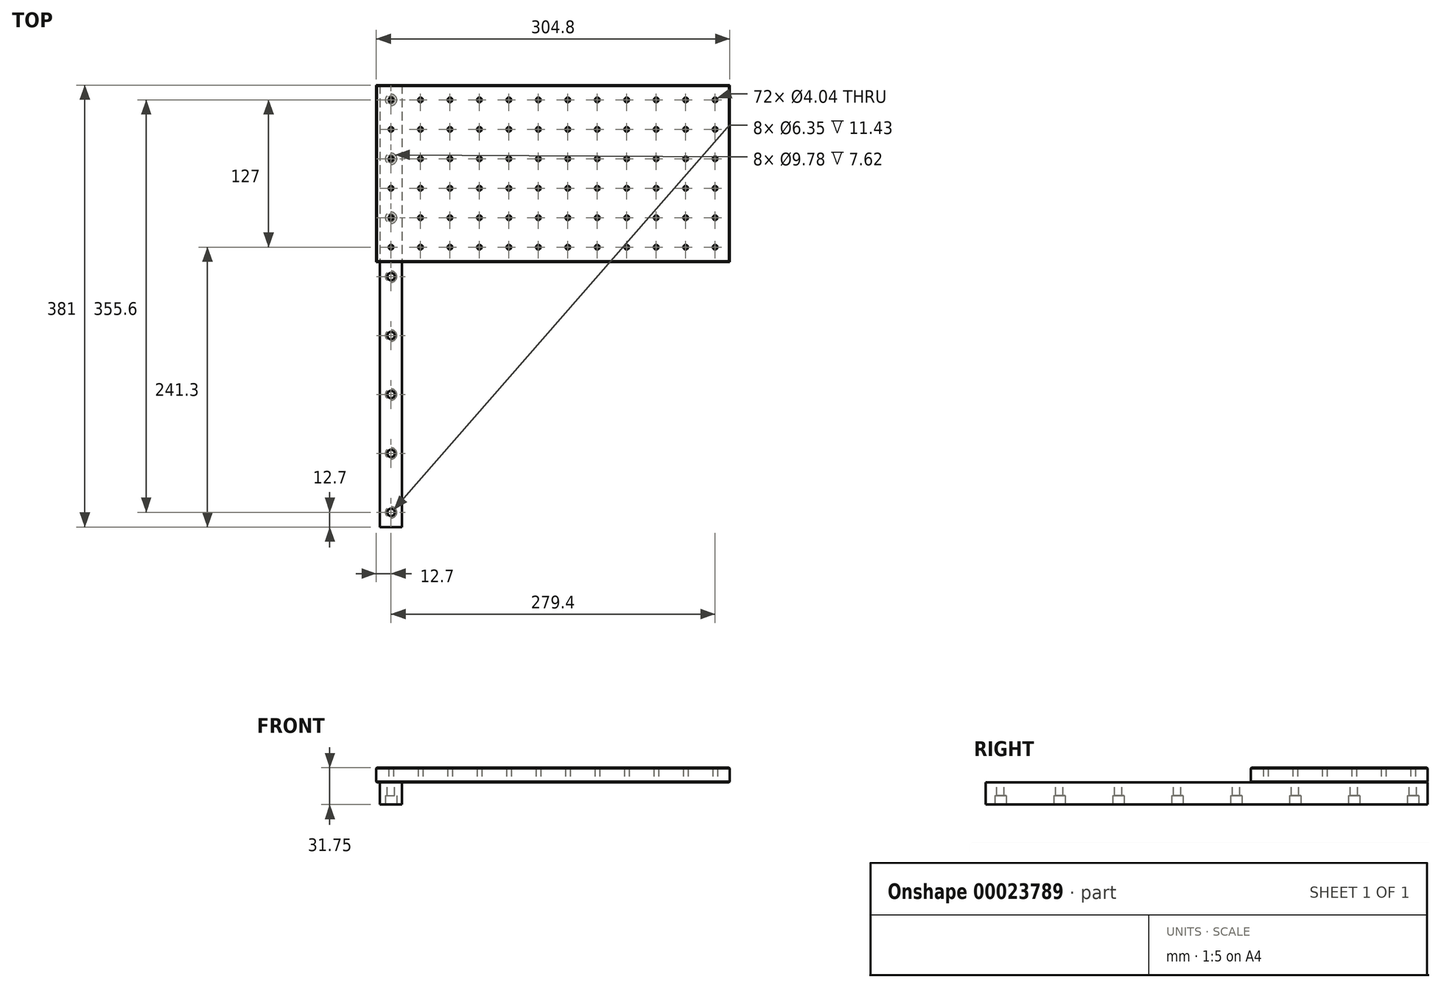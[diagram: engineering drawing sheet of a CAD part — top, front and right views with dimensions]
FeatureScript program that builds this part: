
annotation { "Feature Type Name" : "Feature", "Feature Type Description" : "" }
export const myFeature = defineFeature(function(context is Context, id is Id, definition is map)
    precondition{}
    {
        {
            var Q0;
            Q0=qCreatedBy(makeId("Top.planeOp"),FACE);
            var sketch = newSketch(context, id + "F0", { "sketchPlane" : qUnion([Q0])});
            skLineSegment(sketch, "E0.bottom", {"start": v(0, 0) * mm, "end": v(304.8, 0) * mm});
            skLineSegment(sketch, "E0.top", {"start": v(0, 152.4) * mm, "end": v(304.8, 152.4) * mm});
            skLineSegment(sketch, "E0.left", {"start": v(0, 0) * mm, "end": v(0, 152.4) * mm});
            skLineSegment(sketch, "E0.right", {"start": v(304.8, 0) * mm, "end": v(304.8, 152.4) * mm});
            skCircle(sketch, "E1", {"center": v(12.7, 139.7) * mm, "radius": 2.02 * mm});
            skCircle(sketch, "E2.0.1.0", {"center": v(12.7, 114.3) * mm, "radius": 2.02 * mm});
            skCircle(sketch, "E2.0.2.0", {"center": v(12.7, 88.9) * mm, "radius": 2.02 * mm});
            skCircle(sketch, "E2.0.3.0", {"center": v(12.7, 63.5) * mm, "radius": 2.02 * mm});
            skCircle(sketch, "E2.0.4.0", {"center": v(12.7, 38.1) * mm, "radius": 2.02 * mm});
            skCircle(sketch, "E2.0.5.0", {"center": v(12.7, 12.7) * mm, "radius": 2.02 * mm});
            skCircle(sketch, "E2.1.0.0", {"center": v(38.1, 139.7) * mm, "radius": 2.02 * mm});
            skCircle(sketch, "E2.1.1.0", {"center": v(38.1, 114.3) * mm, "radius": 2.02 * mm});
            skCircle(sketch, "E2.1.2.0", {"center": v(38.1, 88.9) * mm, "radius": 2.02 * mm});
            skCircle(sketch, "E2.1.3.0", {"center": v(38.1, 63.5) * mm, "radius": 2.02 * mm});
            skCircle(sketch, "E2.1.4.0", {"center": v(38.1, 38.1) * mm, "radius": 2.02 * mm});
            skCircle(sketch, "E2.1.5.0", {"center": v(38.1, 12.7) * mm, "radius": 2.02 * mm});
            skCircle(sketch, "E2.2.0.0", {"center": v(63.5, 139.7) * mm, "radius": 2.02 * mm});
            skCircle(sketch, "E2.2.1.0", {"center": v(63.5, 114.3) * mm, "radius": 2.02 * mm});
            skCircle(sketch, "E2.2.2.0", {"center": v(63.5, 88.9) * mm, "radius": 2.02 * mm});
            skCircle(sketch, "E2.2.3.0", {"center": v(63.5, 63.5) * mm, "radius": 2.02 * mm});
            skCircle(sketch, "E2.2.4.0", {"center": v(63.5, 38.1) * mm, "radius": 2.02 * mm});
            skCircle(sketch, "E2.2.5.0", {"center": v(63.5, 12.7) * mm, "radius": 2.02 * mm});
            skCircle(sketch, "E2.3.0.0", {"center": v(88.9, 139.7) * mm, "radius": 2.02 * mm});
            skCircle(sketch, "E2.3.1.0", {"center": v(88.9, 114.3) * mm, "radius": 2.02 * mm});
            skCircle(sketch, "E2.3.2.0", {"center": v(88.9, 88.9) * mm, "radius": 2.02 * mm});
            skCircle(sketch, "E2.3.3.0", {"center": v(88.9, 63.5) * mm, "radius": 2.02 * mm});
            skCircle(sketch, "E2.3.4.0", {"center": v(88.9, 38.1) * mm, "radius": 2.02 * mm});
            skCircle(sketch, "E2.3.5.0", {"center": v(88.9, 12.7) * mm, "radius": 2.02 * mm});
            skCircle(sketch, "E2.4.0.0", {"center": v(114.3, 139.7) * mm, "radius": 2.02 * mm});
            skCircle(sketch, "E2.4.1.0", {"center": v(114.3, 114.3) * mm, "radius": 2.02 * mm});
            skCircle(sketch, "E2.4.2.0", {"center": v(114.3, 88.9) * mm, "radius": 2.02 * mm});
            skCircle(sketch, "E2.4.3.0", {"center": v(114.3, 63.5) * mm, "radius": 2.02 * mm});
            skCircle(sketch, "E2.4.4.0", {"center": v(114.3, 38.1) * mm, "radius": 2.02 * mm});
            skCircle(sketch, "E2.4.5.0", {"center": v(114.3, 12.7) * mm, "radius": 2.02 * mm});
            skCircle(sketch, "E2.5.0.0", {"center": v(139.7, 139.7) * mm, "radius": 2.02 * mm});
            skCircle(sketch, "E2.5.1.0", {"center": v(139.7, 114.3) * mm, "radius": 2.02 * mm});
            skCircle(sketch, "E2.5.2.0", {"center": v(139.7, 88.9) * mm, "radius": 2.02 * mm});
            skCircle(sketch, "E2.5.3.0", {"center": v(139.7, 63.5) * mm, "radius": 2.02 * mm});
            skCircle(sketch, "E2.5.4.0", {"center": v(139.7, 38.1) * mm, "radius": 2.02 * mm});
            skCircle(sketch, "E2.5.5.0", {"center": v(139.7, 12.7) * mm, "radius": 2.02 * mm});
            skCircle(sketch, "E2.6.0.0", {"center": v(165.1, 139.7) * mm, "radius": 2.02 * mm});
            skCircle(sketch, "E2.6.1.0", {"center": v(165.1, 114.3) * mm, "radius": 2.02 * mm});
            skCircle(sketch, "E2.6.2.0", {"center": v(165.1, 88.9) * mm, "radius": 2.02 * mm});
            skCircle(sketch, "E2.6.3.0", {"center": v(165.1, 63.5) * mm, "radius": 2.02 * mm});
            skCircle(sketch, "E2.6.4.0", {"center": v(165.1, 38.1) * mm, "radius": 2.02 * mm});
            skCircle(sketch, "E2.6.5.0", {"center": v(165.1, 12.7) * mm, "radius": 2.02 * mm});
            skCircle(sketch, "E2.7.0.0", {"center": v(190.5, 139.7) * mm, "radius": 2.02 * mm});
            skCircle(sketch, "E2.7.1.0", {"center": v(190.5, 114.3) * mm, "radius": 2.02 * mm});
            skCircle(sketch, "E2.7.2.0", {"center": v(190.5, 88.9) * mm, "radius": 2.02 * mm});
            skCircle(sketch, "E2.7.3.0", {"center": v(190.5, 63.5) * mm, "radius": 2.02 * mm});
            skCircle(sketch, "E2.7.4.0", {"center": v(190.5, 38.1) * mm, "radius": 2.02 * mm});
            skCircle(sketch, "E2.7.5.0", {"center": v(190.5, 12.7) * mm, "radius": 2.02 * mm});
            skCircle(sketch, "E2.8.0.0", {"center": v(215.9, 139.7) * mm, "radius": 2.02 * mm});
            skCircle(sketch, "E2.8.1.0", {"center": v(215.9, 114.3) * mm, "radius": 2.02 * mm});
            skCircle(sketch, "E2.8.2.0", {"center": v(215.9, 88.9) * mm, "radius": 2.02 * mm});
            skCircle(sketch, "E2.8.3.0", {"center": v(215.9, 63.5) * mm, "radius": 2.02 * mm});
            skCircle(sketch, "E2.8.4.0", {"center": v(215.9, 38.1) * mm, "radius": 2.02 * mm});
            skCircle(sketch, "E2.8.5.0", {"center": v(215.9, 12.7) * mm, "radius": 2.02 * mm});
            skCircle(sketch, "E2.9.0.0", {"center": v(241.3, 139.7) * mm, "radius": 2.02 * mm});
            skCircle(sketch, "E2.9.1.0", {"center": v(241.3, 114.3) * mm, "radius": 2.02 * mm});
            skCircle(sketch, "E2.9.2.0", {"center": v(241.3, 88.9) * mm, "radius": 2.02 * mm});
            skCircle(sketch, "E2.9.3.0", {"center": v(241.3, 63.5) * mm, "radius": 2.02 * mm});
            skCircle(sketch, "E2.9.4.0", {"center": v(241.3, 38.1) * mm, "radius": 2.02 * mm});
            skCircle(sketch, "E2.9.5.0", {"center": v(241.3, 12.7) * mm, "radius": 2.02 * mm});
            skCircle(sketch, "E2.10.0.0", {"center": v(266.7, 139.7) * mm, "radius": 2.02 * mm});
            skCircle(sketch, "E2.10.1.0", {"center": v(266.7, 114.3) * mm, "radius": 2.02 * mm});
            skCircle(sketch, "E2.10.2.0", {"center": v(266.7, 88.9) * mm, "radius": 2.02 * mm});
            skCircle(sketch, "E2.10.3.0", {"center": v(266.7, 63.5) * mm, "radius": 2.02 * mm});
            skCircle(sketch, "E2.10.4.0", {"center": v(266.7, 38.1) * mm, "radius": 2.02 * mm});
            skCircle(sketch, "E2.10.5.0", {"center": v(266.7, 12.7) * mm, "radius": 2.02 * mm});
            skCircle(sketch, "E2.11.0.0", {"center": v(292.1, 139.7) * mm, "radius": 2.02 * mm});
            skCircle(sketch, "E2.11.1.0", {"center": v(292.1, 114.3) * mm, "radius": 2.02 * mm});
            skCircle(sketch, "E2.11.2.0", {"center": v(292.1, 88.9) * mm, "radius": 2.02 * mm});
            skCircle(sketch, "E2.11.3.0", {"center": v(292.1, 63.5) * mm, "radius": 2.02 * mm});
            skCircle(sketch, "E2.11.4.0", {"center": v(292.1, 38.1) * mm, "radius": 2.02 * mm});
            skCircle(sketch, "E2.11.5.0", {"center": v(292.1, 12.7) * mm, "radius": 2.02 * mm});
            skLineSegment(sketch, "E2.direction1", {"start": v(6.35, 146.05) * mm, "end": v(31.75, 146.05) * mm, "construction": true});
            skLineSegment(sketch, "E2.direction2", {"start": v(6.35, 146.05) * mm, "end": v(6.35, 120.65) * mm, "construction": true});
            skSolve(sketch);
        }
        {
            var Q0;
            Q0 = qSketchRegion(id + "F0", true);
            extrude(context, id + "F1", {"entities" : qUnion([Q0]), "depth" : 12.7 * mm});
        }
        {
            var Q0;
            Q0=makeQuery(id+"F1.opExtrude","CAP_FACE",FACE,{"disambiguationData":[OSD([sQuery(id+"F0.wireOp",EDGE,"E0.bottom"),sQuery(id+"F0.wireOp",EDGE,"E0.top"),sQuery(id+"F0.wireOp",EDGE,"E0.left"),sQuery(id+"F0.wireOp",EDGE,"E0.right"),sQuery(id+"F0.wireOp",EDGE,"E1"),sQuery(id+"F0.wireOp",EDGE,"E2.0.1.0"),sQuery(id+"F0.wireOp",EDGE,"E2.0.2.0"),sQuery(id+"F0.wireOp",EDGE,"E2.0.3.0"),sQuery(id+"F0.wireOp",EDGE,"E2.0.4.0"),sQuery(id+"F0.wireOp",EDGE,"E2.0.5.0"),sQuery(id+"F0.wireOp",EDGE,"E2.1.0.0"),sQuery(id+"F0.wireOp",EDGE,"E2.1.1.0"),sQuery(id+"F0.wireOp",EDGE,"E2.1.2.0"),sQuery(id+"F0.wireOp",EDGE,"E2.1.3.0"),sQuery(id+"F0.wireOp",EDGE,"E2.1.4.0"),sQuery(id+"F0.wireOp",EDGE,"E2.1.5.0"),sQuery(id+"F0.wireOp",EDGE,"E2.2.0.0"),sQuery(id+"F0.wireOp",EDGE,"E2.2.1.0"),sQuery(id+"F0.wireOp",EDGE,"E2.2.2.0"),sQuery(id+"F0.wireOp",EDGE,"E2.2.3.0"),sQuery(id+"F0.wireOp",EDGE,"E2.2.4.0"),sQuery(id+"F0.wireOp",EDGE,"E2.2.5.0"),sQuery(id+"F0.wireOp",EDGE,"E2.3.0.0"),sQuery(id+"F0.wireOp",EDGE,"E2.3.1.0"),sQuery(id+"F0.wireOp",EDGE,"E2.3.2.0"),sQuery(id+"F0.wireOp",EDGE,"E2.3.3.0"),sQuery(id+"F0.wireOp",EDGE,"E2.3.4.0"),sQuery(id+"F0.wireOp",EDGE,"E2.3.5.0"),sQuery(id+"F0.wireOp",EDGE,"E2.4.0.0"),sQuery(id+"F0.wireOp",EDGE,"E2.4.1.0"),sQuery(id+"F0.wireOp",EDGE,"E2.4.2.0"),sQuery(id+"F0.wireOp",EDGE,"E2.4.3.0"),sQuery(id+"F0.wireOp",EDGE,"E2.4.4.0"),sQuery(id+"F0.wireOp",EDGE,"E2.4.5.0"),sQuery(id+"F0.wireOp",EDGE,"E2.5.0.0"),sQuery(id+"F0.wireOp",EDGE,"E2.5.1.0"),sQuery(id+"F0.wireOp",EDGE,"E2.5.2.0"),sQuery(id+"F0.wireOp",EDGE,"E2.5.3.0"),sQuery(id+"F0.wireOp",EDGE,"E2.5.4.0"),sQuery(id+"F0.wireOp",EDGE,"E2.5.5.0"),sQuery(id+"F0.wireOp",EDGE,"E2.6.0.0"),sQuery(id+"F0.wireOp",EDGE,"E2.6.1.0"),sQuery(id+"F0.wireOp",EDGE,"E2.6.2.0"),sQuery(id+"F0.wireOp",EDGE,"E2.6.3.0"),sQuery(id+"F0.wireOp",EDGE,"E2.6.4.0"),sQuery(id+"F0.wireOp",EDGE,"E2.6.5.0"),sQuery(id+"F0.wireOp",EDGE,"E2.7.0.0"),sQuery(id+"F0.wireOp",EDGE,"E2.7.1.0"),sQuery(id+"F0.wireOp",EDGE,"E2.7.2.0"),sQuery(id+"F0.wireOp",EDGE,"E2.7.3.0"),sQuery(id+"F0.wireOp",EDGE,"E2.7.4.0"),sQuery(id+"F0.wireOp",EDGE,"E2.7.5.0"),sQuery(id+"F0.wireOp",EDGE,"E2.8.0.0"),sQuery(id+"F0.wireOp",EDGE,"E2.8.1.0"),sQuery(id+"F0.wireOp",EDGE,"E2.8.2.0"),sQuery(id+"F0.wireOp",EDGE,"E2.8.3.0"),sQuery(id+"F0.wireOp",EDGE,"E2.8.4.0"),sQuery(id+"F0.wireOp",EDGE,"E2.8.5.0"),sQuery(id+"F0.wireOp",EDGE,"E2.9.0.0"),sQuery(id+"F0.wireOp",EDGE,"E2.9.1.0"),sQuery(id+"F0.wireOp",EDGE,"E2.9.2.0"),sQuery(id+"F0.wireOp",EDGE,"E2.9.3.0"),sQuery(id+"F0.wireOp",EDGE,"E2.9.4.0"),sQuery(id+"F0.wireOp",EDGE,"E2.9.5.0"),sQuery(id+"F0.wireOp",EDGE,"E2.10.0.0"),sQuery(id+"F0.wireOp",EDGE,"E2.10.1.0"),sQuery(id+"F0.wireOp",EDGE,"E2.10.2.0"),sQuery(id+"F0.wireOp",EDGE,"E2.10.3.0"),sQuery(id+"F0.wireOp",EDGE,"E2.10.4.0"),sQuery(id+"F0.wireOp",EDGE,"E2.10.5.0"),sQuery(id+"F0.wireOp",EDGE,"E2.11.0.0"),sQuery(id+"F0.wireOp",EDGE,"E2.11.1.0"),sQuery(id+"F0.wireOp",EDGE,"E2.11.2.0"),sQuery(id+"F0.wireOp",EDGE,"E2.11.3.0"),sQuery(id+"F0.wireOp",EDGE,"E2.11.4.0"),sQuery(id+"F0.wireOp",EDGE,"E2.11.5.0")])],"isStart":true});
            var sketch = newSketch(context, id + "F2", { "sketchPlane" : qUnion([Q0])});
            skLineSegment(sketch, "E3.bottom", {"start": v(-3.18, -152.4) * mm, "end": v(22.22, -152.4) * mm});
            skLineSegment(sketch, "E3.top", {"start": v(3.17, 228.6) * mm, "end": v(22.22, 228.6) * mm});
            skLineSegment(sketch, "E3.left", {"start": v(3.17, -152.4) * mm, "end": v(3.17, 228.6) * mm});
            skLineSegment(sketch, "E3.right", {"start": v(22.22, -152.4) * mm, "end": v(22.22, 228.6) * mm});
            skCircle(sketch, "E4", {"center": v(12.7, -139.7) * mm, "radius": 3.18 * mm});
            skCircle(sketch, "E5.0.1.0", {"center": v(12.7, -88.9) * mm, "radius": 3.18 * mm});
            skCircle(sketch, "E5.0.2.0", {"center": v(12.7, -38.1) * mm, "radius": 3.18 * mm});
            skCircle(sketch, "E5.0.3.0", {"center": v(12.7, 12.7) * mm, "radius": 3.18 * mm});
            skCircle(sketch, "E5.0.4.0", {"center": v(12.7, 63.5) * mm, "radius": 3.18 * mm});
            skCircle(sketch, "E5.0.5.0", {"center": v(12.7, 114.3) * mm, "radius": 3.18 * mm});
            skCircle(sketch, "E5.0.6.0", {"center": v(12.7, 165.1) * mm, "radius": 3.18 * mm});
            skLineSegment(sketch, "E5.direction1", {"start": v(12.7, -139.7) * mm, "end": v(38.1, -139.7) * mm, "construction": true});
            skLineSegment(sketch, "E5.direction2", {"start": v(12.7, -139.7) * mm, "end": v(12.7, -88.9) * mm, "construction": true});
            skCircle(sketch, "E6.0.0.7", {"center": v(12.7, 215.9) * mm, "radius": 3.18 * mm});
            skSolve(sketch);
        }
        {
            var Q0;
            Q0 = qSketchRegion(id + "F2", true);
            extrude(context, id + "F3", {"entities" : qUnion([Q0]), "depth" : 19.05 * mm});
        }
        {
            var Q0;
            Q0=makeQuery(id+"F3.opExtrude","CAP_FACE",FACE,{"disambiguationData":[OSD([sQuery(id+"F2.wireOp",EDGE,"E3.bottom"),sQuery(id+"F2.wireOp",EDGE,"E3.top"),sQuery(id+"F2.wireOp",EDGE,"E3.left"),sQuery(id+"F2.wireOp",EDGE,"E3.right"),sQuery(id+"F2.wireOp",EDGE,"E4"),sQuery(id+"F2.wireOp",EDGE,"E5.0.1.0"),sQuery(id+"F2.wireOp",EDGE,"E5.0.2.0"),sQuery(id+"F2.wireOp",EDGE,"E5.0.3.0"),sQuery(id+"F2.wireOp",EDGE,"E5.0.4.0"),sQuery(id+"F2.wireOp",EDGE,"E5.0.5.0"),sQuery(id+"F2.wireOp",EDGE,"E5.0.6.0"),sQuery(id+"F2.wireOp",EDGE,"E6.0.0.7")])],"isStart":false});
            var sketch = newSketch(context, id + "F4", { "sketchPlane" : qUnion([Q0])});
            skCircle(sketch, "E7", {"center": v(12.7, -139.7) * mm, "radius": 4.89 * mm});
            skCircle(sketch, "E8.0.1.0", {"center": v(12.7, -88.9) * mm, "radius": 4.89 * mm});
            skCircle(sketch, "E8.0.2.0", {"center": v(12.7, -38.1) * mm, "radius": 4.89 * mm});
            skCircle(sketch, "E8.0.3.0", {"center": v(12.7, 12.7) * mm, "radius": 4.89 * mm});
            skCircle(sketch, "E8.0.4.0", {"center": v(12.7, 63.5) * mm, "radius": 4.89 * mm});
            skCircle(sketch, "E8.0.5.0", {"center": v(12.7, 114.3) * mm, "radius": 4.89 * mm});
            skCircle(sketch, "E8.0.6.0", {"center": v(12.7, 165.1) * mm, "radius": 4.89 * mm});
            skCircle(sketch, "E8.0.7.0", {"center": v(12.7, 215.9) * mm, "radius": 4.89 * mm});
            skLineSegment(sketch, "E8.direction1", {"start": v(12.7, -139.7) * mm, "end": v(38.1, -139.7) * mm, "construction": true});
            skLineSegment(sketch, "E8.direction2", {"start": v(12.7, -139.7) * mm, "end": v(12.7, -88.9) * mm, "construction": true});
            skSolve(sketch);
        }
        {
            var Q0;
            Q0 = qSketchRegion(id + "F4", true);
            extrude(context, id + "F5", {"entities" : qUnion([Q0]), "operationType" : NewBodyOperationType.REMOVE, "oppositeDirection" : true, "depth" : 7.62 * mm});
        }
        {
            var Q0;
            Q0=makeQuery(id+"F1.opExtrude","CAP_EDGE",EDGE,{"disambiguationData":[OSD([sQuery(id+"F0.wireOp",EDGE,"E0.top")])],"isStart":false});
            var Q1;
            Q1=makeQuery(id+"F1.opExtrude","CAP_EDGE",EDGE,{"disambiguationData":[OSD([sQuery(id+"F0.wireOp",EDGE,"E0.right")])],"isStart":false});
            var Q2;
            Q2=makeQuery(id+"F1.opExtrude","CAP_EDGE",EDGE,{"disambiguationData":[OSD([sQuery(id+"F0.wireOp",EDGE,"E0.bottom")])],"isStart":false});
            var Q3;
            Q3=makeQuery(id+"F1.opExtrude","CAP_EDGE",EDGE,{"disambiguationData":[OSD([sQuery(id+"F0.wireOp",EDGE,"E0.left")])],"isStart":false});
            var Q4;
            Q4=makeQuery(id+"F1.opExtrude","CAP_EDGE",EDGE,{"disambiguationData":[OSD([sQuery(id+"F0.wireOp",EDGE,"E0.left")])],"isStart":true});
            var Q5;
            Q5=makeQuery(id+"F1.opExtrude","CAP_EDGE",EDGE,{"disambiguationData":[OSD([sQuery(id+"F0.wireOp",EDGE,"E0.top")])],"isStart":true});
            var Q6;
            Q6=makeQuery(id+"F1.opExtrude","CAP_EDGE",EDGE,{"disambiguationData":[OSD([sQuery(id+"F0.wireOp",EDGE,"E0.right")])],"isStart":true});
            var Q7;
            Q7=makeQuery(id+"F1.opExtrude","CAP_EDGE",EDGE,{"disambiguationData":[OSD([sQuery(id+"F0.wireOp",EDGE,"E0.bottom")])],"isStart":true});
            chamfer(context, id + "F6", {"entities" : qUnion([Q0, Q1, Q2, Q3, Q4, Q5, Q6, Q7]), "width" : 0.64 * mm});
        }
    });
